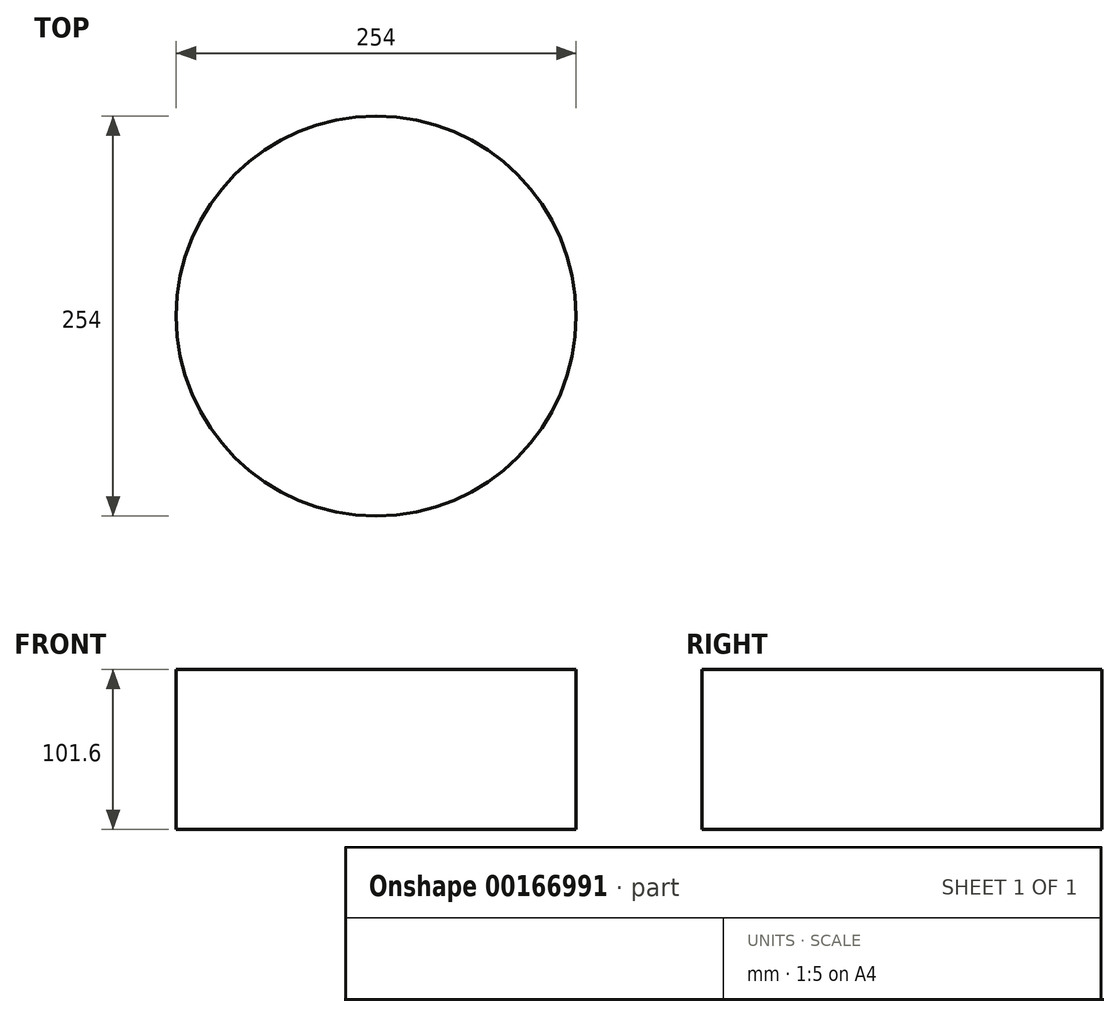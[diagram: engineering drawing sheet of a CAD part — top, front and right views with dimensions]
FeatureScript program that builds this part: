
annotation { "Feature Type Name" : "Feature", "Feature Type Description" : "" }
export const myFeature = defineFeature(function(context is Context, id is Id, definition is map)
    precondition{}
    {
        {
            var Q0;
            Q0=qCreatedBy(makeId("Top.planeOp"),FACE);
            var sketch = newSketch(context, id + "F0", { "sketchPlane" : qUnion([Q0])});
            skCircle(sketch, "E0", {"center": v(0, 0) * mm, "radius": 127 * mm});
            skSolve(sketch);
        }
        {
            var Q0;
            Q0 = qSketchRegion(id + "F0", true);
            extrude(context, id + "F1", {"entities" : qUnion([Q0]), "depth" : 101.6 * mm});
        }
    });
